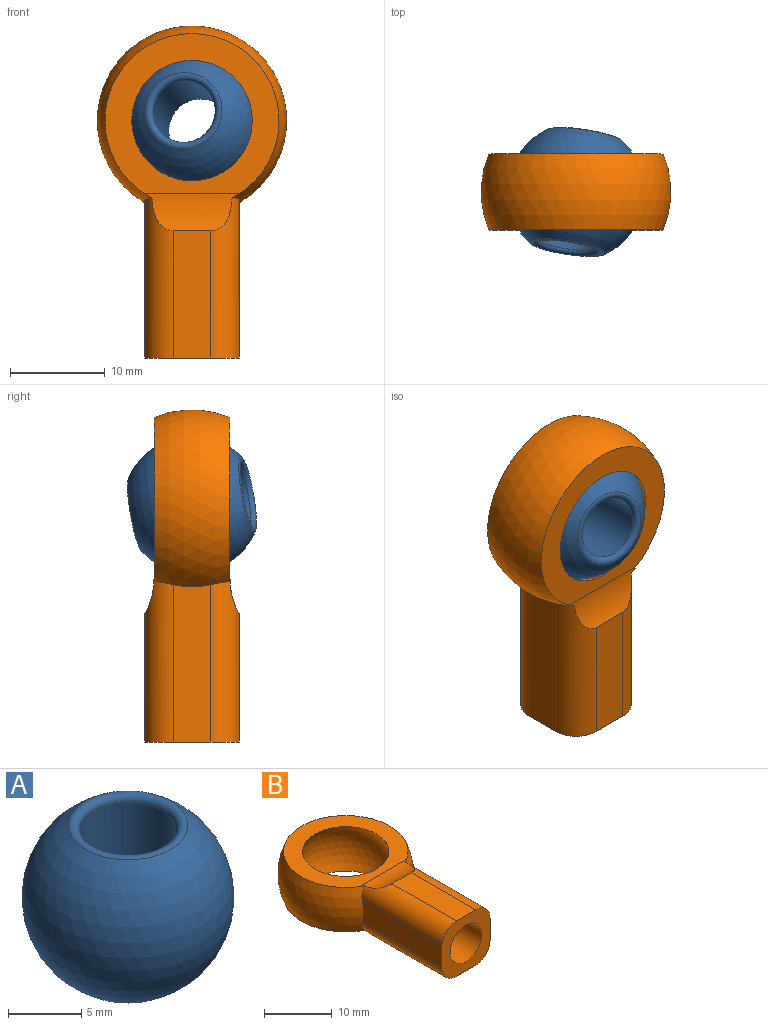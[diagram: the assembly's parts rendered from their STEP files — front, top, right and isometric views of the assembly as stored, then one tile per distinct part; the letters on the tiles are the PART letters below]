
ASSEMBLY  parts=2 mates=1
PART A: 4 faces, bbox 14.5x14.5x12.2 mm
  f0: sphere r=7.25mm, area 545.9mm2, adj f2,f3
  f1: cylinder r=3.3mm len=11.16mm, axis (0,0,-1), area 231.3mm2, adj f2,f3
  f2: torus R=3.8mm, axis (0,0,1), area 24.6mm2, adj f0,f1
  f3: torus R=3.8mm, axis (0,0,-1), area 24.6mm2, adj f0,f1
PART B: 17 faces, bbox 20x35x10 mm
  f0: plane 13.4x4mm, normal (0,0,-1), area 53.6mm2, adj f4,f6,f7,f12
  f1: sphere r=10mm, area 418.6mm2, adj f2,f3,f6,f7,f8,f9,f10,f11
  f2: plane 16.57x4mm, normal (1,0,0), area 65.7mm2, adj f1,f4,f7,f9
  f3: plane 16.57x4mm, normal (-1,0,0), area 65.7mm2, adj f1,f4,f6,f8
  f4: plane 10x10mm, normal (0,-1,0), area 58.1mm2, adj f0,f2,f3,f5,f6,f7,f8,f9
  f5: plane 13.4x4mm, normal (0,0,1), area 53.6mm2, adj f4,f8,f9,f13
  f6: cylinder r=3mm len=16.87mm, axis (0,-1,0), area 72.6mm2, adj f0,f1,f3,f4,f12
  f7: cylinder r=3mm len=16.87mm, axis (0,1,0), area 72.6mm2, adj f0,f1,f2,f4,f12
  f8: cylinder r=3mm len=16.87mm, axis (0,1,0), area 72.6mm2, adj f1,f3,f4,f5,f13
  f9: cylinder r=3mm len=16.87mm, axis (0,-1,0), area 72.6mm2, adj f1,f2,f4,f5,f13
  f10: plane 18.33x16.89mm, normal (0,0,1), area 127.8mm2, adj f1,f13,f14
  f11: plane 18.33x16.89mm, normal (0,0,-1), area 127.8mm2, adj f1,f12,f14
  f12: cylinder r=8mm len=9.86mm, axis (1,0,0), area 31mm2, adj f0,f1,f6,f7,f11
  f13: cylinder r=8mm len=9.86mm, axis (-1,0,0), area 31mm2, adj f1,f5,f8,f9,f10
  f14: sphere r=7.5mm, area 377mm2, adj f10,f11
  f15: cylinder r=3.3mm len=12.5mm, axis (0,-1,0), area 259.2mm2, adj f4,f16
  f16: plane 6.6x6.6mm, normal (0,-1,0), area 34.2mm2, adj f15
PLACE A rot(axis=(0.97,0.04,-0.22),82.6deg) t=(0,0,25)mm
PLACE B rot(axis=(1,0,0),90deg) t=(0,0,25)mm
MATE ball A.f1 <-> B.f14  axis (-0.15,-0.97,0.17) through (0,0,25)mm
